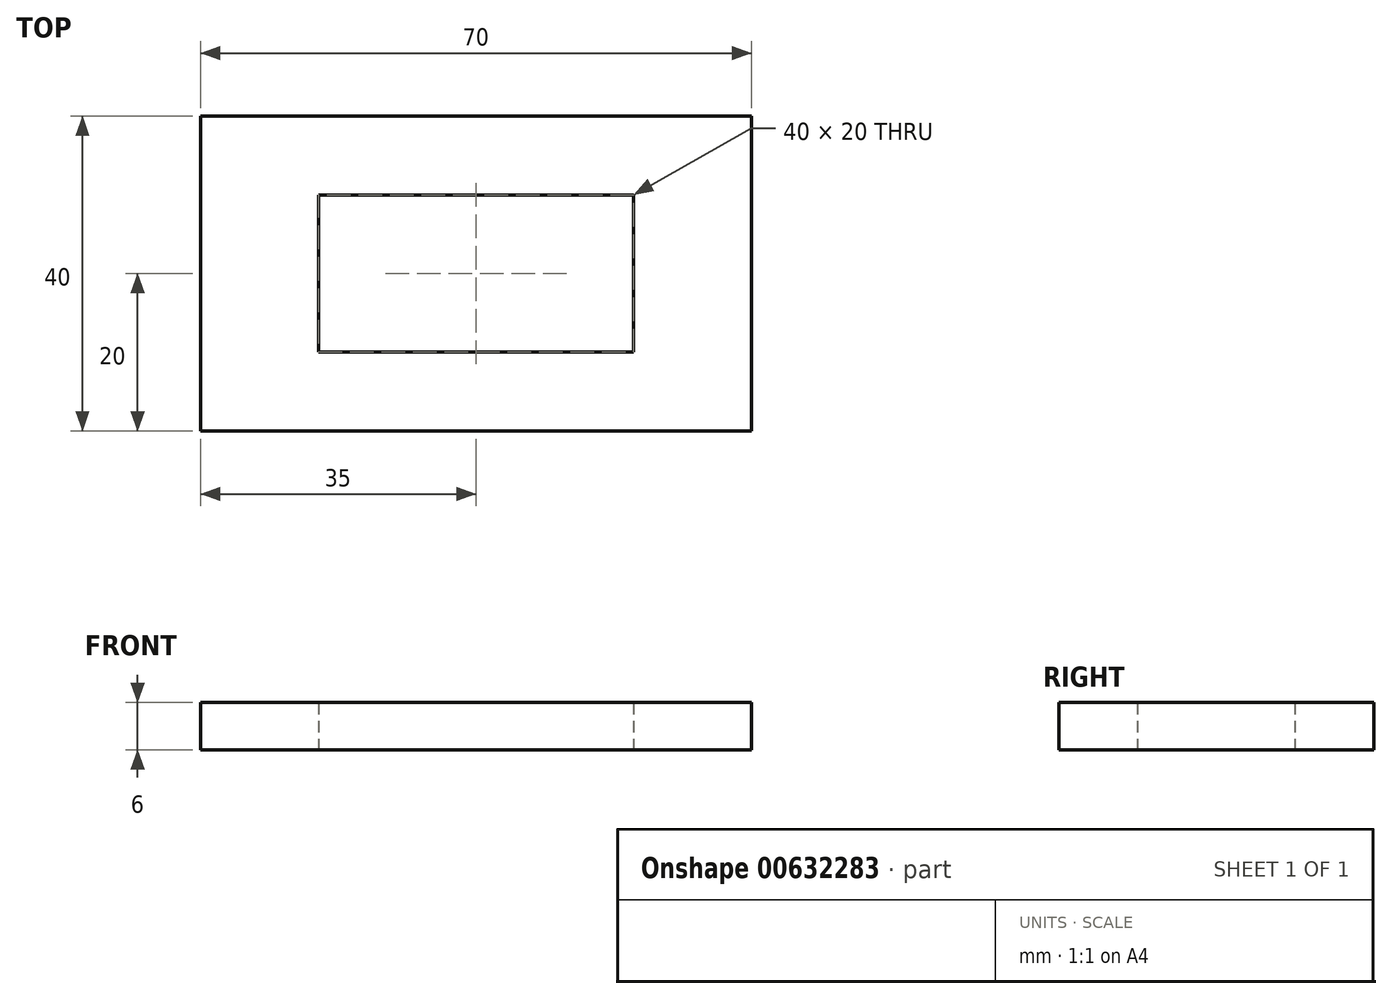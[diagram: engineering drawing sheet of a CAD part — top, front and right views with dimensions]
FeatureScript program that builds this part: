
annotation { "Feature Type Name" : "Feature", "Feature Type Description" : "" }
export const myFeature = defineFeature(function(context is Context, id is Id, definition is map)
    precondition{}
    {
        {
            var Q0;
            Q0=qCreatedBy(makeId("Top.planeOp"),FACE);
            var sketch = newSketch(context, id + "F0", { "sketchPlane" : qUnion([Q0])});
            skLineSegment(sketch, "E0.bottom", {"start": v(35, -20) * mm, "end": v(-35, -20) * mm});
            skLineSegment(sketch, "E0.top", {"start": v(35, 20) * mm, "end": v(-35, 20) * mm});
            skLineSegment(sketch, "E0.left", {"start": v(35, -20) * mm, "end": v(35, 20) * mm});
            skLineSegment(sketch, "E0.right", {"start": v(-35, -20) * mm, "end": v(-35, 20) * mm});
            skPoint(sketch, "E0.middle", {"position": v(0, 0) * mm});
            skLineSegment(sketch, "E1.bottom", {"start": v(20, -10) * mm, "end": v(-20, -10) * mm});
            skLineSegment(sketch, "E1.top", {"start": v(20, 10) * mm, "end": v(-20, 10) * mm});
            skLineSegment(sketch, "E1.left", {"start": v(20, -10) * mm, "end": v(20, 10) * mm});
            skLineSegment(sketch, "E1.right", {"start": v(-20, -10) * mm, "end": v(-20, 10) * mm});
            skSolve(sketch);
        }
        {
            var Q0;
            Q0 = qSketchRegion(id + "F0", true);
            extrude(context, id + "F1", {"entities" : qUnion([Q0]), "depth" : 6 * mm, "offsetDistance" : 25 * mm});
        }
    });
